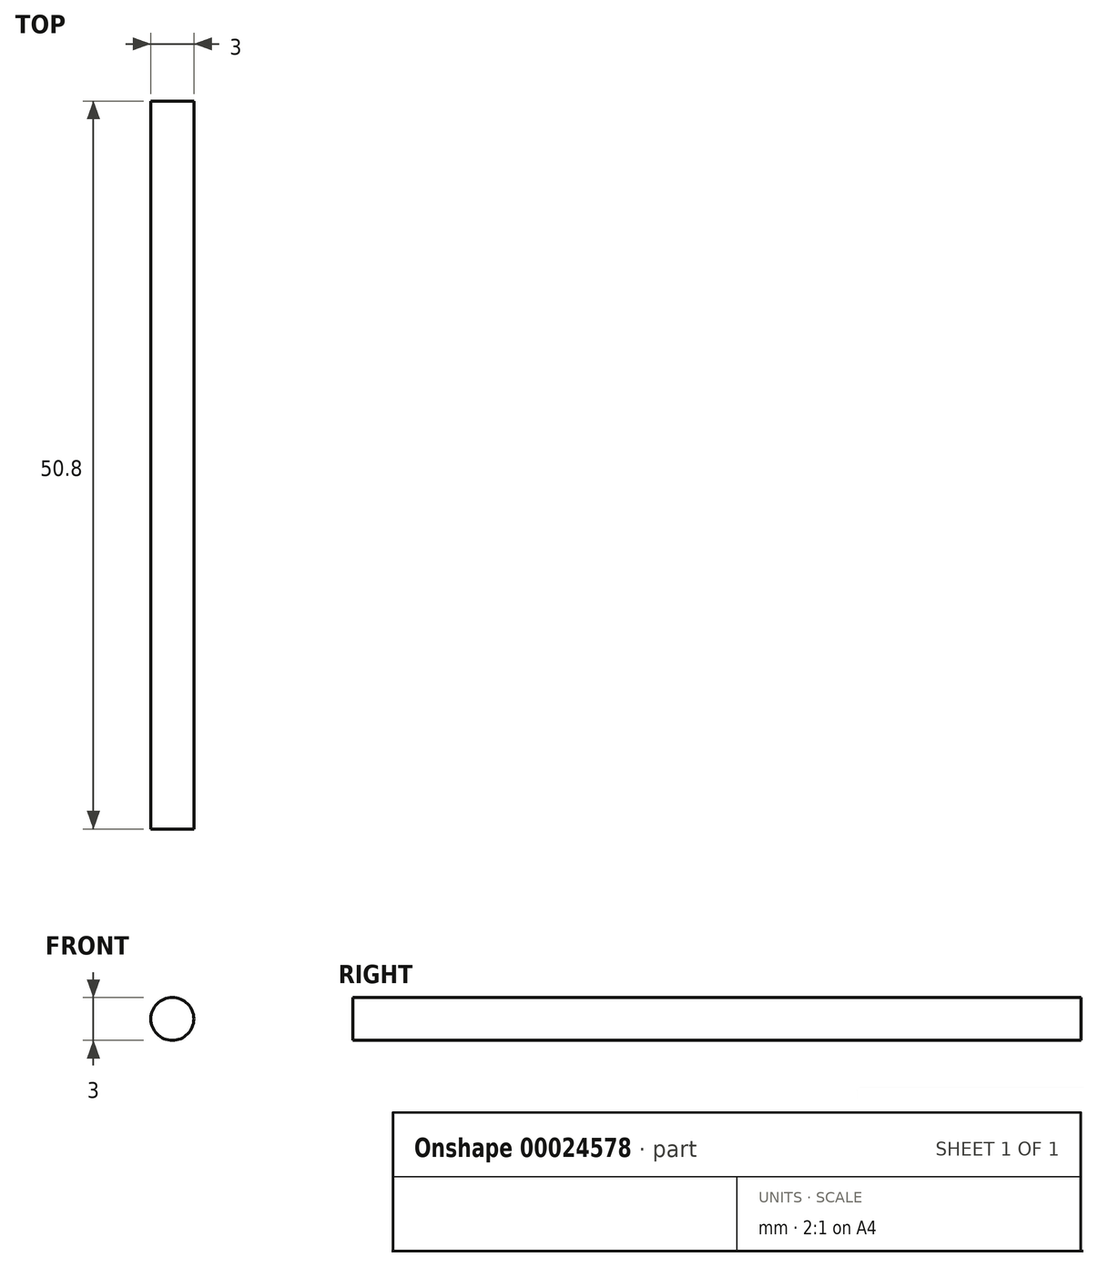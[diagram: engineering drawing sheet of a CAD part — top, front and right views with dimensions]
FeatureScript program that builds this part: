
annotation { "Feature Type Name" : "Feature", "Feature Type Description" : "" }
export const myFeature = defineFeature(function(context is Context, id is Id, definition is map)
    precondition{}
    {
        {
            var Q0;
            Q0=qCreatedBy(makeId("Front.planeOp"),FACE);
            var sketch = newSketch(context, id + "F0", { "sketchPlane" : qUnion([Q0])});
            skCircle(sketch, "E0", {"center": v(-19.37, 8.5) * mm, "radius": 1.5 * mm});
            skSolve(sketch);
        }
        {
            var Q0;
            Q0=makeQuery(id+"F0.imprint","IMPRINT",FACE,{"disambiguationData":[TD([[makeQuery(id+"F0.imprint","IMPRINT",EDGE,{"derivedFrom":sQuery(id+"F0.wireOp",EDGE,"E0")}),1.0]])]});
            extrude(context, id + "F1", {"entities" : qUnion([Q0]), "depth" : 50.8 * mm});
        }
    });
